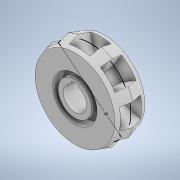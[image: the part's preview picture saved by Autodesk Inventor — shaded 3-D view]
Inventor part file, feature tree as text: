
AUTODESK INVENTOR PART (.ipt)
format: ipt  version: 2020.2 (Build 242310000, 310)  size: 201,728 bytes
history: native  units: mm
features: sketch x6, extrude x4, mirror x1, revolve x1, pattern_circular x1
ambient origin geometry x8: Origin, YZ Plane, XZ Plane, XY Plane, X Axis, Y Axis, Z Axis, Center Point
bodies: Solid1 (feature_tree)
feature tree (13):
  extrude  "Extrusion1"  Depth=17.0mm TaperAngle=0.0deg
  extrude  "Extrusion2"  Depth=3.5mm
  extrude  "Extrusion3"  TaperAngle=0.0deg  [1 undecoded]
  mirror  "Mirror1"
  revolve  "Revolution1"  [1 undecoded]
  extrude  "Extrusion4"  Depth=2.5mm
  pattern_circular  "Circular Pattern1"  [2 undecoded]
  sketch  "Sketch6"  dims[d13=90.0deg d14=13.0mm d15=12.0mm d16=12.0mm d17=0.0mm d18=80.0mm d19=360.0deg d21=46.0mm]
  sketch  "Sketch1"  dims[d0=45.0mm d1=17.0mm d2=0.0mm]
  sketch  "Sketch2"  dims[d3=13.2mm d4=3.5mm]
  sketch  "Sketch3"  dims[d5=1.5mm d6=0.0mm d7=0.0mm]
  sketch  "Sketch4"  dims[d8=19.0mm d9=3.0mm]
  sketch  "Sketch5"  dims[d10=6.0mm d11=0.0mm d12=2.5mm]
note: 4 required parameter values undecoded (feature->parameter linkage not recoverable at this tier; creation-order binding heuristic only, values carry confidence <= 0.55)